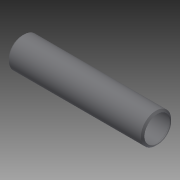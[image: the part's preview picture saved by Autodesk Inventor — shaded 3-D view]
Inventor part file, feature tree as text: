
AUTODESK INVENTOR PART (.ipt)
format: ipt  version: 2014 (Build 180170000, 170)  size: 123,904 bytes
history: native  units: in
note: dims shown in document units (in); Inventor stores cm internally (conversion verified against a paired STEP export)
features: other x56, revolve x1, sketch x1
ambient origin geometry x8: Origin, YZ Plane, XZ Plane, XY Plane, X Axis, Y Axis, Z Axis, Center Point
bodies: Solid1 (feature_tree)
feature tree (58):
  revolve  "Revolution1"  [1 undecoded]
  other  "o1_XY"
  other  "o1_YZ"
  other  "o1_ZX"
  other  "o1_X"
  other  "o1_Y"
  other  "o1_Z"
  other  "o1_Center"
  other  "o2_XY"
  other  "o2_YZ"
  other  "o2_ZX"
  other  "o2_X"
  other  "o2_Y"
  other  "o2_Z"
  other  "o2_Center"
  other  "t1_XY"
  other  "t1_YZ"
  other  "t1_ZX"
  other  "t1_X"
  other  "t1_Y"
  other  "t1_Z"
  other  "t1_Center"
  other  "t2_XY"
  other  "t2_YZ"
  other  "t2_ZX"
  other  "t2_X"
  other  "t2_Y"
  other  "t2_Z"
  other  "t2_Center"
  other  "t3_XY"
  other  "t3_YZ"
  other  "t3_ZX"
  other  "t3_X"
  other  "t3_Y"
  other  "t3_Z"
  other  "t3_Center"
  other  "t4_XY"
  other  "t4_YZ"
  other  "t4_ZX"
  other  "t4_X"
  other  "t4_Y"
  other  "t4_Z"
  other  "t4_Center"
  other  "tube1_XY"
  other  "tube1_YZ"
  other  "tube1_ZX"
  other  "tube1_X"
  other  "tube1_Y"
  other  "tube1_Z"
  other  "tube1_Center"
  other  "tube2_XY"
  other  "tube2_YZ"
  other  "tube2_ZX"
  other  "tube2_X"
  other  "tube2_Y"
  other  "tube2_Z"
  other  "tube2_Center"
  sketch  "Sketch_5"  dims[d0=360.0deg]
note: 1 required parameter value undecoded (feature->parameter linkage not recoverable at this tier; creation-order binding heuristic only, values carry confidence <= 0.55)
